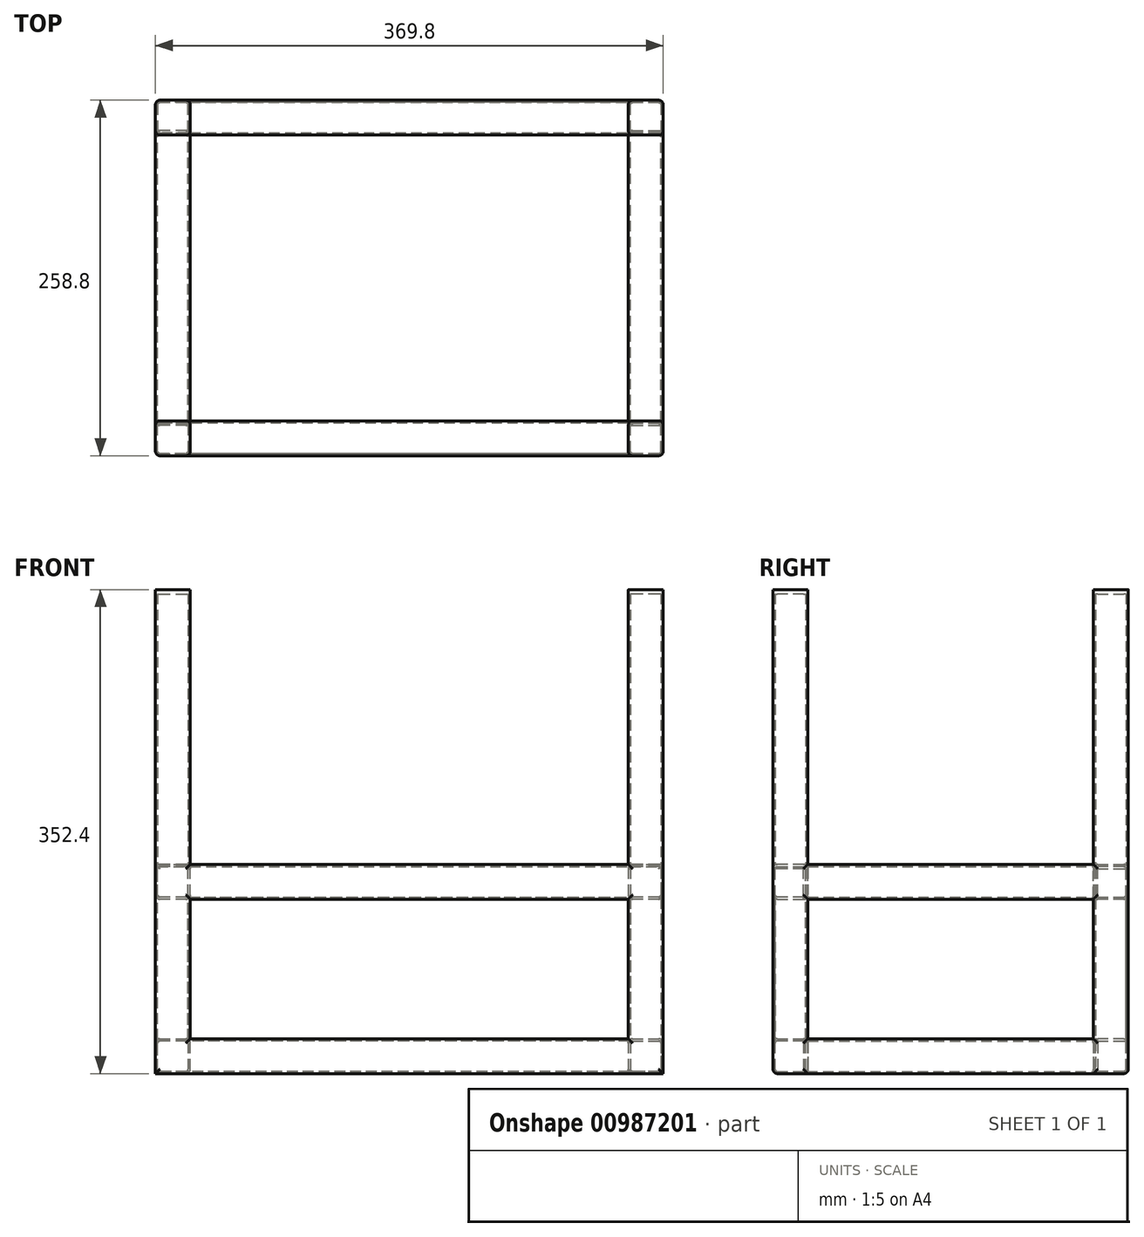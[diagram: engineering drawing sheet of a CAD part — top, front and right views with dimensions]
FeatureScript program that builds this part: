
annotation { "Feature Type Name" : "Feature", "Feature Type Description" : "" }
export const myFeature = defineFeature(function(context is Context, id is Id, definition is map)
    precondition{}
    {
        {
            var Q0;
            Q0=qCreatedBy(makeId("Front.planeOp"),FACE);
            var sketch = newSketch(context, id + "F0", { "sketchPlane" : qUnion([Q0])});
            skLineSegment(sketch, "E0.bottom", {"start": v(-184.9, 76.2) * mm, "end": v(184.9, 76.2) * mm});
            skLineSegment(sketch, "E0.top", {"start": v(-184.9, -76.2) * mm, "end": v(184.9, -76.2) * mm});
            skLineSegment(sketch, "E0.left", {"start": v(-184.9, 76.2) * mm, "end": v(-184.9, -76.2) * mm});
            skLineSegment(sketch, "E0.right", {"start": v(184.9, 76.2) * mm, "end": v(184.9, -76.2) * mm});
            skLineSegment(sketch, "E1", {"start": v(-184.9, 76.2) * mm, "end": v(-184.9, 164.2) * mm});
            skLineSegment(sketch, "E2", {"start": v(184.9, 76.2) * mm, "end": v(184.9, 164.2) * mm});
            skSolve(sketch);
        }
        {
            var Q0;
            Q0=qCreatedBy(makeId("Top.planeOp"),FACE);
            var sketch = newSketch(context, id + "F1", { "sketchPlane" : qUnion([Q0])});
            skPoint(sketch, "E3.0", {"position": v(-184.9, 0) * mm});
            skLineSegment(sketch, "E4.bottom", {"start": v(-181.73, -12.7) * mm, "end": v(-162.68, -12.7) * mm});
            skLineSegment(sketch, "E4.top", {"start": v(-181.73, 12.7) * mm, "end": v(-162.68, 12.7) * mm});
            skLineSegment(sketch, "E4.left", {"start": v(-184.9, -9.53) * mm, "end": v(-184.9, 9.53) * mm});
            skLineSegment(sketch, "E4.right", {"start": v(-159.5, -9.53) * mm, "end": v(-159.5, 9.53) * mm});
            skPoint(sketch, "E5.visualSharp", {"position": v(-184.9, -12.7) * mm});
            skArc(sketch, "E5.filletArc", {"start": v(-184.9, -9.53) * mm, "mid": v(-183.97, -11.77) * mm, "end": v(-181.73, -12.7) * mm});
            skPoint(sketch, "E6.visualSharp", {"position": v(-159.5, -12.7) * mm});
            skArc(sketch, "E6.filletArc", {"start": v(-162.68, -12.7) * mm, "mid": v(-160.43, -11.77) * mm, "end": v(-159.5, -9.53) * mm});
            skPoint(sketch, "E7.visualSharp", {"position": v(-159.5, 12.7) * mm});
            skArc(sketch, "E7.filletArc", {"start": v(-159.5, 9.53) * mm, "mid": v(-160.43, 11.77) * mm, "end": v(-162.68, 12.7) * mm});
            skPoint(sketch, "E8.visualSharp", {"position": v(-184.9, 12.7) * mm});
            skArc(sketch, "E8.filletArc", {"start": v(-181.73, 12.7) * mm, "mid": v(-183.97, 11.77) * mm, "end": v(-184.9, 9.53) * mm});
            skArc(sketch, "E9.0", {"start": v(-183.31, -9.53) * mm, "mid": v(-182.85, -10.65) * mm, "end": v(-181.73, -11.11) * mm});
            skLineSegment(sketch, "E9.1", {"start": v(-183.31, -9.53) * mm, "end": v(-183.31, 9.53) * mm});
            skLineSegment(sketch, "E9.2", {"start": v(-181.73, -11.11) * mm, "end": v(-162.68, -11.11) * mm});
            skArc(sketch, "E9.3", {"start": v(-181.73, 11.11) * mm, "mid": v(-182.85, 10.65) * mm, "end": v(-183.31, 9.53) * mm});
            skArc(sketch, "E9.4", {"start": v(-162.68, -11.11) * mm, "mid": v(-161.55, -10.65) * mm, "end": v(-161.09, -9.53) * mm});
            skLineSegment(sketch, "E9.5", {"start": v(-161.09, -9.53) * mm, "end": v(-161.09, 9.53) * mm});
            skArc(sketch, "E9.6", {"start": v(-161.09, 9.53) * mm, "mid": v(-161.55, 10.65) * mm, "end": v(-162.68, 11.11) * mm});
            skLineSegment(sketch, "E9.7", {"start": v(-181.73, 11.11) * mm, "end": v(-162.68, 11.11) * mm});
            skSolve(sketch);
        }
        {
            var Q0;
            Q0=makeQuery(id+"F1.imprint","IMPRINT",FACE,{"disambiguationData":[TD([[makeQuery(id+"F1.imprint","IMPRINT",EDGE,{"derivedFrom":sQuery(id+"F1.wireOp",EDGE,"E4.bottom")}),1.0]])]});
            var Q1;
            Q1=sQuery(id+"F0.wireOp",EDGE,"E0.left");
            var Q2;
            Q2=sQuery(id+"F0.wireOp",EDGE,"E0.bottom");
            var Q3;
            Q3=sQuery(id+"F0.wireOp",EDGE,"E0.top");
            var Q4;
            Q4=sQuery(id+"F0.wireOp",EDGE,"E0.right");
            sweep(context, id + "F2", {"profiles" : qUnion([Q0]), "path" : qUnion([Q1, Q2, Q3, Q4])});
        }
        {
            var Q0;
            Q0=makeQuery(id+"F2.opSweep","SWEPT_FACE",FACE,{"disambiguationData":[OSD([sQuery(id+"F0.wireOp",EDGE,"E0.bottom"),sQuery(id+"F1.wireOp",EDGE,"E4.left")])]});
            var sketch = newSketch(context, id + "F3", { "sketchPlane" : qUnion([Q0])});
            skPoint(sketch, "E10.0", {"position": v(-184.9, 0) * mm});
            skLineSegment(sketch, "E11.bottom", {"start": v(-181.72, -12.7) * mm, "end": v(-162.68, -12.7) * mm});
            skLineSegment(sketch, "E11.top", {"start": v(-181.72, 12.7) * mm, "end": v(-162.68, 12.7) * mm});
            skLineSegment(sketch, "E11.left", {"start": v(-184.9, -9.53) * mm, "end": v(-184.9, 9.53) * mm});
            skLineSegment(sketch, "E11.right", {"start": v(-159.5, -9.53) * mm, "end": v(-159.5, 9.53) * mm});
            skPoint(sketch, "E12.visualSharp", {"position": v(-184.9, -12.7) * mm});
            skArc(sketch, "E12.filletArc", {"start": v(-184.9, -9.53) * mm, "mid": v(-183.97, -11.77) * mm, "end": v(-181.72, -12.7) * mm});
            skPoint(sketch, "E13.visualSharp", {"position": v(-159.5, -12.7) * mm});
            skArc(sketch, "E13.filletArc", {"start": v(-162.68, -12.7) * mm, "mid": v(-160.43, -11.77) * mm, "end": v(-159.5, -9.53) * mm});
            skPoint(sketch, "E14.visualSharp", {"position": v(-159.5, 12.7) * mm});
            skArc(sketch, "E14.filletArc", {"start": v(-159.5, 9.53) * mm, "mid": v(-160.43, 11.77) * mm, "end": v(-162.68, 12.7) * mm});
            skPoint(sketch, "E15.visualSharp", {"position": v(-184.9, 12.7) * mm});
            skArc(sketch, "E15.filletArc", {"start": v(-181.72, 12.7) * mm, "mid": v(-183.97, 11.77) * mm, "end": v(-184.9, 9.53) * mm});
            skArc(sketch, "E16.0", {"start": v(-183.31, -9.53) * mm, "mid": v(-182.85, -10.65) * mm, "end": v(-181.72, -11.11) * mm});
            skLineSegment(sketch, "E16.1", {"start": v(-183.31, -9.53) * mm, "end": v(-183.31, 9.53) * mm});
            skLineSegment(sketch, "E16.2", {"start": v(-181.72, -11.11) * mm, "end": v(-162.68, -11.11) * mm});
            skArc(sketch, "E16.3", {"start": v(-181.72, 11.11) * mm, "mid": v(-182.85, 10.65) * mm, "end": v(-183.31, 9.53) * mm});
            skArc(sketch, "E16.4", {"start": v(-162.68, -11.11) * mm, "mid": v(-161.55, -10.65) * mm, "end": v(-161.09, -9.53) * mm});
            skLineSegment(sketch, "E16.5", {"start": v(-161.09, -9.53) * mm, "end": v(-161.09, 9.53) * mm});
            skArc(sketch, "E16.6", {"start": v(-161.09, 9.53) * mm, "mid": v(-161.55, 10.65) * mm, "end": v(-162.68, 11.11) * mm});
            skLineSegment(sketch, "E16.7", {"start": v(-181.72, 11.11) * mm, "end": v(-162.68, 11.11) * mm});
            skLineSegment(sketch, "E17.0", {"start": v(-181.73, 12.7) * mm, "end": v(181.72, 12.7) * mm});
            skSolve(sketch);
        }
        {
            var Q0;
            {var subQ0=sQuery(id+"F3.wireOp",EDGE,"E11.left");Q0=makeQuery(id+"F3.imprint","IMPRINT",FACE,{"disambiguationData":[TD([[makeQuery(id+"F3.imprint","IMPRINT",EDGE,{"derivedFrom":subQ0}),1.0]])]});}
            var Q1;
            Q1=makeQuery(id+"F3.imprint","IMPRINT",FACE,{"disambiguationData":[TD([[makeQuery(id+"F3.imprint","IMPRINT",EDGE,{"derivedFrom":sQuery(id+"F3.wireOp",EDGE,"E11.top")}),-1.0]])]});
            var Q2;
            {var subQ0=sQuery(id+"F3.wireOp",EDGE,"E11.right");Q2=makeQuery(id+"F3.imprint","IMPRINT",FACE,{"disambiguationData":[TD([[makeQuery(id+"F3.imprint","IMPRINT",EDGE,{"derivedFrom":subQ0}),1.0]])]});}
            var Q3;
            Q3=makeQuery(id+"F3.imprint","IMPRINT",FACE,{"disambiguationData":[TD([[makeQuery(id+"F3.imprint","IMPRINT",EDGE,{"derivedFrom":sQuery(id+"F3.wireOp",EDGE,"E11.bottom")}),1.0]])]});
            var Q4;
            Q4=makeQuery(id+"F2.opSweep","SWEPT_BODY",BODY,{"disambiguationData":[OSD([sQuery(id+"F0.wireOp",EDGE,"E0.bottom"),sQuery(id+"F1.wireOp",EDGE,"E4.bottom"),sQuery(id+"F1.wireOp",EDGE,"E4.top"),sQuery(id+"F1.wireOp",EDGE,"E4.left"),sQuery(id+"F1.wireOp",EDGE,"E4.right"),sQuery(id+"F1.wireOp",EDGE,"E5.filletArc"),sQuery(id+"F1.wireOp",EDGE,"E6.filletArc"),sQuery(id+"F1.wireOp",EDGE,"E7.filletArc"),sQuery(id+"F1.wireOp",EDGE,"E8.filletArc"),sQuery(id+"F1.wireOp",EDGE,"E9.0"),sQuery(id+"F1.wireOp",EDGE,"E9.1"),sQuery(id+"F1.wireOp",EDGE,"E9.2"),sQuery(id+"F1.wireOp",EDGE,"E9.3"),sQuery(id+"F1.wireOp",EDGE,"E9.4"),sQuery(id+"F1.wireOp",EDGE,"E9.5"),sQuery(id+"F1.wireOp",EDGE,"E9.6"),sQuery(id+"F1.wireOp",EDGE,"E9.7")])]});
            extrude(context, id + "F4", {"entities" : qUnion([Q0, Q1, Q2, Q3]), "depth" : 200 * mm, "offsetDistance" : 25.4 * mm, "hasSecondDirection" : true, "secondDirectionOppositeDirection" : true, "secondDirectionDepth" : 3.17 * mm, "secondDirectionBoundEntityBody" : qUnion([Q4])});
        }
        {
            var Q0;
            Q0=makeQuery(id+"F4.opExtrude","CAP_FACE",FACE,{"disambiguationData":[OSD([sQuery(id+"F3.wireOp",EDGE,"E11.bottom"),sQuery(id+"F3.wireOp",EDGE,"E11.top"),sQuery(id+"F3.wireOp",EDGE,"E11.left"),sQuery(id+"F3.wireOp",EDGE,"E11.right"),sQuery(id+"F3.wireOp",EDGE,"E12.filletArc"),sQuery(id+"F3.wireOp",EDGE,"E13.filletArc"),sQuery(id+"F3.wireOp",EDGE,"E14.filletArc"),sQuery(id+"F3.wireOp",EDGE,"E15.filletArc"),sQuery(id+"F3.wireOp",EDGE,"E16.0"),sQuery(id+"F3.wireOp",EDGE,"E16.1"),sQuery(id+"F3.wireOp",EDGE,"E16.2"),sQuery(id+"F3.wireOp",EDGE,"E16.3"),sQuery(id+"F3.wireOp",EDGE,"E16.4"),sQuery(id+"F3.wireOp",EDGE,"E16.5"),sQuery(id+"F3.wireOp",EDGE,"E16.6"),sQuery(id+"F3.wireOp",EDGE,"E16.7")])],"isStart":false});
            var sketch = newSketch(context, id + "F5", { "sketchPlane" : qUnion([Q0])});
            skLineSegment(sketch, "E18.0.0", {"start": v(-184.9, 9.52) * mm, "end": v(-184.9, -9.53) * mm});
            skArc(sketch, "E18.0.1", {"start": v(-184.9, -9.53) * mm, "mid": v(-183.97, -11.77) * mm, "end": v(-181.72, -12.7) * mm});
            skLineSegment(sketch, "E18.0.2", {"start": v(-181.72, -12.7) * mm, "end": v(-162.68, -12.7) * mm});
            skArc(sketch, "E18.0.3", {"start": v(-162.68, -12.7) * mm, "mid": v(-160.43, -11.77) * mm, "end": v(-159.5, -9.53) * mm});
            skLineSegment(sketch, "E18.0.4", {"start": v(-159.5, -9.53) * mm, "end": v(-159.5, 9.52) * mm});
            skArc(sketch, "E18.0.5", {"start": v(-159.5, 9.52) * mm, "mid": v(-160.43, 11.77) * mm, "end": v(-162.68, 12.7) * mm});
            skLineSegment(sketch, "E18.0.6", {"start": v(-162.68, 12.7) * mm, "end": v(-181.72, 12.7) * mm});
            skArc(sketch, "E18.0.7", {"start": v(-181.72, 12.7) * mm, "mid": v(-183.97, 11.77) * mm, "end": v(-184.9, 9.52) * mm});
            skSolve(sketch);
        }
        {
            var Q0;
            Q0=makeQuery(id+"F5.imprint","IMPRINT",FACE,{"disambiguationData":[TD([[makeQuery(id+"F5.imprint","IMPRINT",EDGE,{"derivedFrom":sQuery(id+"F5.wireOp",EDGE,"E18.0.0")}),1.0]])]});
            var Q1;
            Q1=makeQuery(id+"F5.imprint","IMPRINT",FACE,{"disambiguationData":[TD([[makeQuery(id+"F5.imprint","IMPRINT",EDGE,{"derivedFrom":makeQuery(id+"F4.opExtrude","CAP_EDGE",EDGE,{"disambiguationData":[OSD([sQuery(id+"F3.wireOp",EDGE,"E16.0")])],"isStart":false})}),1.0]])]});
            extrude(context, id + "F6", {"entities" : qUnion([Q0, Q1]), "operationType" : NewBodyOperationType.ADD, "oppositeDirection" : true, "depth" : 3.17 * mm, "offsetDistance" : 25.4 * mm});
        }
        {
            var Q0;
            Q0=makeQuery(id+"F4.opExtrude","SWEPT_BODY",BODY,{"disambiguationData":[OSD([sQuery(id+"F3.wireOp",EDGE,"E11.bottom"),sQuery(id+"F3.wireOp",EDGE,"E11.top"),sQuery(id+"F3.wireOp",EDGE,"E11.left"),sQuery(id+"F3.wireOp",EDGE,"E11.right"),sQuery(id+"F3.wireOp",EDGE,"E12.filletArc"),sQuery(id+"F3.wireOp",EDGE,"E13.filletArc"),sQuery(id+"F3.wireOp",EDGE,"E14.filletArc"),sQuery(id+"F3.wireOp",EDGE,"E15.filletArc"),sQuery(id+"F3.wireOp",EDGE,"E16.0"),sQuery(id+"F3.wireOp",EDGE,"E16.1"),sQuery(id+"F3.wireOp",EDGE,"E16.2"),sQuery(id+"F3.wireOp",EDGE,"E16.3"),sQuery(id+"F3.wireOp",EDGE,"E16.4"),sQuery(id+"F3.wireOp",EDGE,"E16.5"),sQuery(id+"F3.wireOp",EDGE,"E16.6"),sQuery(id+"F3.wireOp",EDGE,"E16.7")])]});
            var Q1;
            Q1=makeQuery(id+"F6.opExtrude","SWEPT_BODY",BODY,{"disambiguationData":[OSD([sQuery(id+"F5.wireOp",EDGE,"E18.0.0"),sQuery(id+"F5.wireOp",EDGE,"E18.0.1"),sQuery(id+"F5.wireOp",EDGE,"E18.0.2"),sQuery(id+"F5.wireOp",EDGE,"E18.0.3"),sQuery(id+"F5.wireOp",EDGE,"E18.0.4"),sQuery(id+"F5.wireOp",EDGE,"E18.0.5"),sQuery(id+"F5.wireOp",EDGE,"E18.0.6"),sQuery(id+"F5.wireOp",EDGE,"E18.0.7")])]});
            var Q2;
            Q2=qCreatedBy(makeId("Right.planeOp"),FACE);
            mirror(context, id + "F7", {"operationType" : NewBodyOperationType.ADD, "entities" : qUnion([Q0, Q1]), "mirrorPlane" : qUnion([Q2])});
        }
        {
            var Q0;
            Q0=qCreatedBy(makeId("Front.planeOp"),FACE);
            cPlane(context, id + "F8", {"entities" : qUnion([Q0]), "cplaneType" : CPlaneType.OFFSET, "offset" : (208 * mm / 2) + 12.7 * mm, "width" : 152.4 * mm, "height" : 152.4 * mm});
        }
        {
            var Q0;
            Q0=makeQuery(id+"F2.opSweep","SWEPT_BODY",BODY,{"disambiguationData":[OSD([sQuery(id+"F0.wireOp",EDGE,"E0.bottom"),sQuery(id+"F1.wireOp",EDGE,"E4.bottom"),sQuery(id+"F1.wireOp",EDGE,"E4.top"),sQuery(id+"F1.wireOp",EDGE,"E4.left"),sQuery(id+"F1.wireOp",EDGE,"E4.right"),sQuery(id+"F1.wireOp",EDGE,"E5.filletArc"),sQuery(id+"F1.wireOp",EDGE,"E6.filletArc"),sQuery(id+"F1.wireOp",EDGE,"E7.filletArc"),sQuery(id+"F1.wireOp",EDGE,"E8.filletArc"),sQuery(id+"F1.wireOp",EDGE,"E9.0"),sQuery(id+"F1.wireOp",EDGE,"E9.1"),sQuery(id+"F1.wireOp",EDGE,"E9.2"),sQuery(id+"F1.wireOp",EDGE,"E9.3"),sQuery(id+"F1.wireOp",EDGE,"E9.4"),sQuery(id+"F1.wireOp",EDGE,"E9.5"),sQuery(id+"F1.wireOp",EDGE,"E9.6"),sQuery(id+"F1.wireOp",EDGE,"E9.7")])]});
            var Q1;
            Q1=qCreatedBy(id+"F8.planeOp",FACE);
            mirror(context, id + "F9", {"entities" : qUnion([Q0]), "mirrorPlane" : qUnion([Q1])});
        }
        {
            var Q0;
            Q0=qCreatedBy(id+"F8.planeOp",FACE);
            var sketch = newSketch(context, id + "F10", { "sketchPlane" : qUnion([Q0])});
            skPoint(sketch, "E19.0", {"position": v(159.5, 63.5) * mm});
            skLineSegment(sketch, "E20.bottom", {"start": v(162.67, 50.8) * mm, "end": v(181.72, 50.8) * mm});
            skLineSegment(sketch, "E20.top", {"start": v(162.67, 76.2) * mm, "end": v(181.72, 76.2) * mm});
            skLineSegment(sketch, "E20.left", {"start": v(159.5, 53.98) * mm, "end": v(159.5, 73.03) * mm});
            skLineSegment(sketch, "E20.right", {"start": v(184.9, 53.98) * mm, "end": v(184.9, 73.03) * mm});
            skPoint(sketch, "E21.visualSharp", {"position": v(159.5, 50.8) * mm});
            skArc(sketch, "E21.filletArc", {"start": v(159.5, 53.98) * mm, "mid": v(160.43, 51.73) * mm, "end": v(162.67, 50.8) * mm});
            skPoint(sketch, "E22.visualSharp", {"position": v(184.9, 50.8) * mm});
            skArc(sketch, "E22.filletArc", {"start": v(181.72, 50.8) * mm, "mid": v(183.97, 51.73) * mm, "end": v(184.9, 53.98) * mm});
            skPoint(sketch, "E23.visualSharp", {"position": v(184.9, 76.2) * mm});
            skArc(sketch, "E23.filletArc", {"start": v(184.9, 73.03) * mm, "mid": v(183.97, 75.27) * mm, "end": v(181.72, 76.2) * mm});
            skPoint(sketch, "E24.visualSharp", {"position": v(159.5, 76.2) * mm});
            skArc(sketch, "E24.filletArc", {"start": v(162.67, 76.2) * mm, "mid": v(160.43, 75.27) * mm, "end": v(159.5, 73.03) * mm});
            skArc(sketch, "E25.0", {"start": v(161.09, 53.98) * mm, "mid": v(161.55, 52.85) * mm, "end": v(162.67, 52.39) * mm});
            skLineSegment(sketch, "E25.1", {"start": v(161.09, 53.98) * mm, "end": v(161.09, 73.03) * mm});
            skLineSegment(sketch, "E25.2", {"start": v(162.67, 52.39) * mm, "end": v(181.72, 52.39) * mm});
            skArc(sketch, "E25.3", {"start": v(162.67, 74.61) * mm, "mid": v(161.55, 74.15) * mm, "end": v(161.09, 73.03) * mm});
            skArc(sketch, "E25.4", {"start": v(181.72, 52.39) * mm, "mid": v(182.85, 52.85) * mm, "end": v(183.31, 53.98) * mm});
            skLineSegment(sketch, "E25.5", {"start": v(183.31, 53.98) * mm, "end": v(183.31, 73.03) * mm});
            skArc(sketch, "E25.6", {"start": v(183.31, 73.03) * mm, "mid": v(182.85, 74.15) * mm, "end": v(181.72, 74.61) * mm});
            skLineSegment(sketch, "E25.7", {"start": v(162.67, 74.61) * mm, "end": v(181.72, 74.61) * mm});
            skSolve(sketch);
        }
        {
            var Q0;
            Q0 = qSketchRegion(id + "F10", true);
            extrude(context, id + "F11", {"entities" : qUnion([Q0]), "depth" : (208 * mm / 2) + 3.17 * mm, "offsetDistance" : 25.4 * mm, "hasSecondDirection" : true, "secondDirectionOppositeDirection" : true, "secondDirectionDepth" : (208 * mm / 2) + 3.17 * mm});
        }
        {
            var Q0;
            Q0=makeQuery(id+"F11.opExtrude","SWEPT_BODY",BODY,{"disambiguationData":[OSD([sQuery(id+"F10.wireOp",EDGE,"E20.bottom"),sQuery(id+"F10.wireOp",EDGE,"E20.top"),sQuery(id+"F10.wireOp",EDGE,"E20.left"),sQuery(id+"F10.wireOp",EDGE,"E20.right"),sQuery(id+"F10.wireOp",EDGE,"E21.filletArc"),sQuery(id+"F10.wireOp",EDGE,"E22.filletArc"),sQuery(id+"F10.wireOp",EDGE,"E23.filletArc"),sQuery(id+"F10.wireOp",EDGE,"E24.filletArc"),sQuery(id+"F10.wireOp",EDGE,"E25.0"),sQuery(id+"F10.wireOp",EDGE,"E25.1"),sQuery(id+"F10.wireOp",EDGE,"E25.2"),sQuery(id+"F10.wireOp",EDGE,"E25.3"),sQuery(id+"F10.wireOp",EDGE,"E25.4"),sQuery(id+"F10.wireOp",EDGE,"E25.5"),sQuery(id+"F10.wireOp",EDGE,"E25.6"),sQuery(id+"F10.wireOp",EDGE,"E25.7")])]});
            var Q1;
            Q1=qCreatedBy(makeId("Right.planeOp"),FACE);
            mirror(context, id + "F12", {"entities" : qUnion([Q0]), "mirrorPlane" : qUnion([Q1])});
        }
        {
            var Q0;
            Q0=makeQuery(id+"F11.opExtrude","SWEPT_BODY",BODY,{"disambiguationData":[OSD([sQuery(id+"F10.wireOp",EDGE,"E20.bottom"),sQuery(id+"F10.wireOp",EDGE,"E20.top"),sQuery(id+"F10.wireOp",EDGE,"E20.left"),sQuery(id+"F10.wireOp",EDGE,"E20.right"),sQuery(id+"F10.wireOp",EDGE,"E21.filletArc"),sQuery(id+"F10.wireOp",EDGE,"E22.filletArc"),sQuery(id+"F10.wireOp",EDGE,"E23.filletArc"),sQuery(id+"F10.wireOp",EDGE,"E24.filletArc"),sQuery(id+"F10.wireOp",EDGE,"E25.0"),sQuery(id+"F10.wireOp",EDGE,"E25.1"),sQuery(id+"F10.wireOp",EDGE,"E25.2"),sQuery(id+"F10.wireOp",EDGE,"E25.3"),sQuery(id+"F10.wireOp",EDGE,"E25.4"),sQuery(id+"F10.wireOp",EDGE,"E25.5"),sQuery(id+"F10.wireOp",EDGE,"E25.6"),sQuery(id+"F10.wireOp",EDGE,"E25.7")])]});
            var Q1;
            Q1=makeQuery(id+"F12.opPattern","COPY",BODY,{"derivedFrom":makeQuery(id+"F11.opExtrude","SWEPT_BODY",BODY,{"disambiguationData":[OSD([sQuery(id+"F10.wireOp",EDGE,"E20.bottom"),sQuery(id+"F10.wireOp",EDGE,"E20.top"),sQuery(id+"F10.wireOp",EDGE,"E20.left"),sQuery(id+"F10.wireOp",EDGE,"E20.right"),sQuery(id+"F10.wireOp",EDGE,"E21.filletArc"),sQuery(id+"F10.wireOp",EDGE,"E22.filletArc"),sQuery(id+"F10.wireOp",EDGE,"E23.filletArc"),sQuery(id+"F10.wireOp",EDGE,"E24.filletArc"),sQuery(id+"F10.wireOp",EDGE,"E25.0"),sQuery(id+"F10.wireOp",EDGE,"E25.1"),sQuery(id+"F10.wireOp",EDGE,"E25.2"),sQuery(id+"F10.wireOp",EDGE,"E25.3"),sQuery(id+"F10.wireOp",EDGE,"E25.4"),sQuery(id+"F10.wireOp",EDGE,"E25.5"),sQuery(id+"F10.wireOp",EDGE,"E25.6"),sQuery(id+"F10.wireOp",EDGE,"E25.7")])]}),"instanceName":"1"});
            var Q2;
            Q2=qCreatedBy(makeId("Top.planeOp"),FACE);
            mirror(context, id + "F13", {"operationType" : NewBodyOperationType.ADD, "entities" : qUnion([Q0, Q1]), "mirrorPlane" : qUnion([Q2])});
        }
    });
